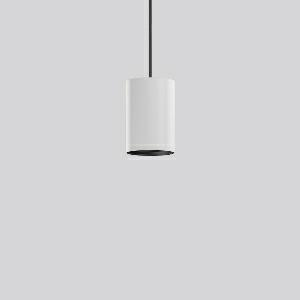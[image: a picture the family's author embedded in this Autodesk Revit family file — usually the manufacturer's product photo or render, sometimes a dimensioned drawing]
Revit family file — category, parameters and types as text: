
# Revit family: deecos_p_maxi_911534_002_76_a176
name_source: partatom
category: Lighting Fixtures
units: mm (PartAtom-declared; Revit-internal decimal feet)

## family parameters
Cut with Voids When Loaded = No
Host = Face
Light Source = No
Part Type = Normal
Room Calculation Point = No
Round Connector Dimension = Use Diameter
Shared = No

## types (1)
- DEECOS P maxi (1 x LED Modul 930, 2750 lm, 3000)
    Apparent Load = 25 VA
    Approval mark = CE
    CIE Flux Codes = 96 100 100 100 100
    Color Rendering = 90
    Color Temperature = 3000
    Default Elevation = 1800 mm
    Description = Series: DEECOS P maxi
Cylindrical pendant luminaire. Housing: die-cast aluminium, powder-coated. Canopy made of powder-coated sheet steel with magnetic attachment. Optical assembly with lens made of plastic (polycarbonate) for the best homogeneous light distribution - can be changed without tools. Best colour rendering index Ra>90. Transparent suspension cable 2 m, can be shortened. High quality converter without flickering and stroboscopic effect. The following accessories can be mounted without use of tools: interchangeable lenses, honeycomb louvre, clear and frosted diffusers, white interchangeable plastic ring. Decorative recessed suspension set available as accessory. 
Colour: traffic white, matt (RAL 9016)
Diameter: 123 mm
Height: 181 mm
Suspension length: 2000 mm
Lamp: LED
Socket: without socket
Colour temperature: 3000K
Colour rendering index (CRI): 92
System power: 25 W
Rated luminous flux: 2750 lm
Luminous efficiency: 110 lm/W
Control gear: Converter, dimmable, DALI
Protection class: I
Type of protection: IP 20
    Height = 181 mm
    Lamp = 1 x LED Modul 930
    Lamp Light Flux = 2750 lm
    Lamp count = 1
    Length = 123 mm
    Lifetime = 50000 h
    Luminous efficacy = 110 lm/W
    Manufacturer = RZB
    ModVariant = No
    Model = 911534.002.76
    Mounting Place = Ceiling
    Mounting Type = Pendant
    Number of Poles = 1
    OnlyDefault = Yes
    Power Factor = 1
    Product Name = DEECOS P maxi
    Product group = Pendant luminaires
    ProductGroupID = 902
    Protection Class = Protection class I
    Protection Degree = IP 20
    RLX_Detail_Level = 1
    RLX_Emergency_Light_Flux = 0 lm
    RLX_Emergency_Type = 0
    RLX_Emergency_Type_DB = No
    RlxData = <blob elided: 35865 chars, md5=c486cbd8>
    Socket = socket
    Standby Power = 0 W
    System Light Flux = 2750 lm
    System Power = 25 W
    Type Comments = Product without accessories
    Type Image = 911480.002.jpg
    URL = http://relux.com
    VarID = ---
    Voltage = 230 V
    Voltage Range = 220-240 V
    Weight = 0.00 kg
    Width = 0 mm  [stored 0 ft]

note: [stored X ft] marks values corroborated as IEEE doubles in the binary element streams (Revit-internal decimal feet)

## geometry (parser evidence)
native form markers: Blend x4, Sweep x10
no freeform markers — native parametric forms only
